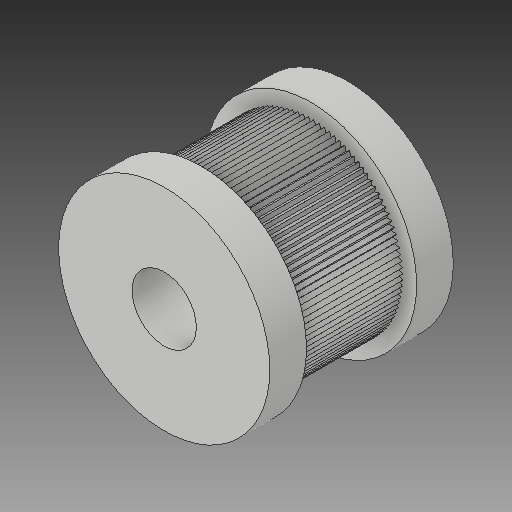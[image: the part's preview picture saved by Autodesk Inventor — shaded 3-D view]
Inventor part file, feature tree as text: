
AUTODESK INVENTOR PART (.ipt)
format: ipt  version: 2019 (Build 230136000, 136)  size: 583,168 bytes
history: native  units: mm
features: extrude x5, sketch x5, pattern_circular x1, plane x1, mirror x1
ambient origin geometry x8: Origin, YZ Plane, XZ Plane, XY Plane, X Axis, Y Axis, Z Axis, Center Point
bodies: Solid1 (feature_tree)
feature tree (13):
  extrude  "Extrusion1"  Depth=20.0mm TaperAngle=0.0deg
  extrude  "Extrusion2"  TaperAngle=30.0deg  [1 undecoded]
  pattern_circular  "Circular Pattern1"  Count=2  [1 undecoded]
  extrude  "Extrusion3"  Depth=1.0mm TaperAngle=360.0deg
  plane  "Work Plane1"
  mirror  "Mirror1"
  extrude  "Extrusion4"  Depth=1.0mm
  extrude  "Extrusion5"  Depth=4.0mm TaperAngle=0.0deg
  sketch  "Sketch1"  dims[d0=20.0mm d1=20.0mm d2=0.0mm]
  sketch  "Sketch2"  dims[d3=30.0deg d9=30.0deg]
  sketch  "Sketch3"  dims[d10=30.0deg]
  sketch  "Sketch4"  dims[d11=0.5mm]
  sketch  "Sketch5"  dims[d12=0.5mm d13=20.0mm d14=0.0mm d15=1080.0mm d16=360.0deg d18=23.0mm d19=4.0mm d20=0.0mm d21=10.0mm d22=7.0mm d23=20.0mm d24=0.0mm d25=15.0mm d26=1.0mm d27=0.0mm]
note: 2 required parameter values undecoded (feature->parameter linkage not recoverable at this tier; creation-order binding heuristic only, values carry confidence <= 0.55)
